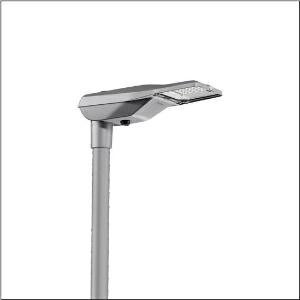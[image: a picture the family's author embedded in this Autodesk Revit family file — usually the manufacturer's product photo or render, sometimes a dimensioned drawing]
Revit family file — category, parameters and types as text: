
# Revit family: streetlight_sl_21_micro___st1_0a_5xe1d33r08db_e2a0
name_source: partatom
category: Lighting Fixtures
units: mm (PartAtom-declared; Revit-internal decimal feet)

## family parameters
Cut with Voids When Loaded = No
Host = Face
Light Source = No
Part Type = Normal
Room Calculation Point = No
Round Connector Dimension = Use Diameter
Shared = No

## types (1)
- --- (1 x LED, 5110 lm, 39.1 W, 3000K)
    Apparent Load = 39 VA
    CIE Flux Codes = 37 72 97 100 100
    Color Rendering = 70
    Color Temperature = 3000K
    Default Elevation = 1800 mm
    Description = Streetlight SL 21 micro, mast luminaire, primary light control with lens, of PMMA, primary optical cover: cover, of toughened safety glass, transparent, light distribution: ST1.0a, light emission: direct distribution, primary light characteristic: asymmetric, installation type: side-entry, post-top, LED, High Power LED, rated luminous flux: 5.110lm, luminous efficacy: 131lm/W, light colour: 730, colour temperature: 3000K, control: flexible luminous flux parameterisation, time-dependent luminous flux control, constant luminous flux control, overheat protection, pre-setting: logarithmic dimming characteristic, mains connection: 220..240V, AC, 50/60Hz, start of lifetime: 39W, end of service life: 41W, reduction: 18W, luminaire housing, of diecast aluminium, powder-coated, Siteco® metallic grey (DB 702S), corrosivity category C5 mid according to DIN EN ISO 12944, please order mast flange separately, inclination adjustable: 0°, 5°, 10°, 15°, sealing non-destructively replaceable, multi-level sealing system, length: 528mm, width: 235mm, height: 110mm, mast flange for spigot size: 42mm (side-entry): 5XC10008XM4, 60/48mm (side-entry/post-top): 5XC10108XM2, 76/60mm (side-entry/post-top): 5XC10108XM1, Smart Interface below, protection rating (complete): IP66, insulation class (complete): insulation class II (safety insulation), certification: CE, ENEC, ENEC+, VDE, impact resistance: IK09, permissible operating ambient temperature for outdoor applications: -40..+50°C, standard-compliant lighting for roads and squares, packaging unit: 1 piece

Light Distribution: ST1.0a
    Height = 110 mm
    Lamp = 1 x LED
    Lamp Light Flux = 5110 lm
    Lamp Power = 39.1 W
    Lamp count = 1
    Length = 528 mm
    Luminous efficacy = 131 lm/W
    Manufacturer = Siteco
    ModVariant = No
    Model = 5XE1D33R08DB
    Number of Poles = 1
    OnlyDefault = Yes
    Power Factor = 1
    Product Name = Streetlight SL 21 micro | ST1.0a
    Product group = mast luminaire | pylon top
    ProductGroupID = 6100
    Protection Class = Protection class II
    Protection Degree = IP 66
    RLX_Detail_Level = 1
    RLX_Emergency_Light_Flux = 0 lm
    RLX_Emergency_Type = 0
    RLX_Emergency_Type_DB = No
    RlxData = <blob elided: 99217 chars, md5=8b11f6ba>
    Socket = socket
    Standby Power = 0 W
    System Light Flux = 5110 lm
    System Power = 39 W
    Type Comments = factory setting: luminous flux: 100 % | dim-lin: 254 | 765 mA
    Type Image = l_1277290.jpg
    URL = http://relux.com
    VarID = @adj_126245
    Voltage = 0 V
    Weight = 0.00 kg
    Width = 235 mm

## geometry (parser evidence)
native form markers: Blend x4, Sweep x11
no freeform markers — native parametric forms only
